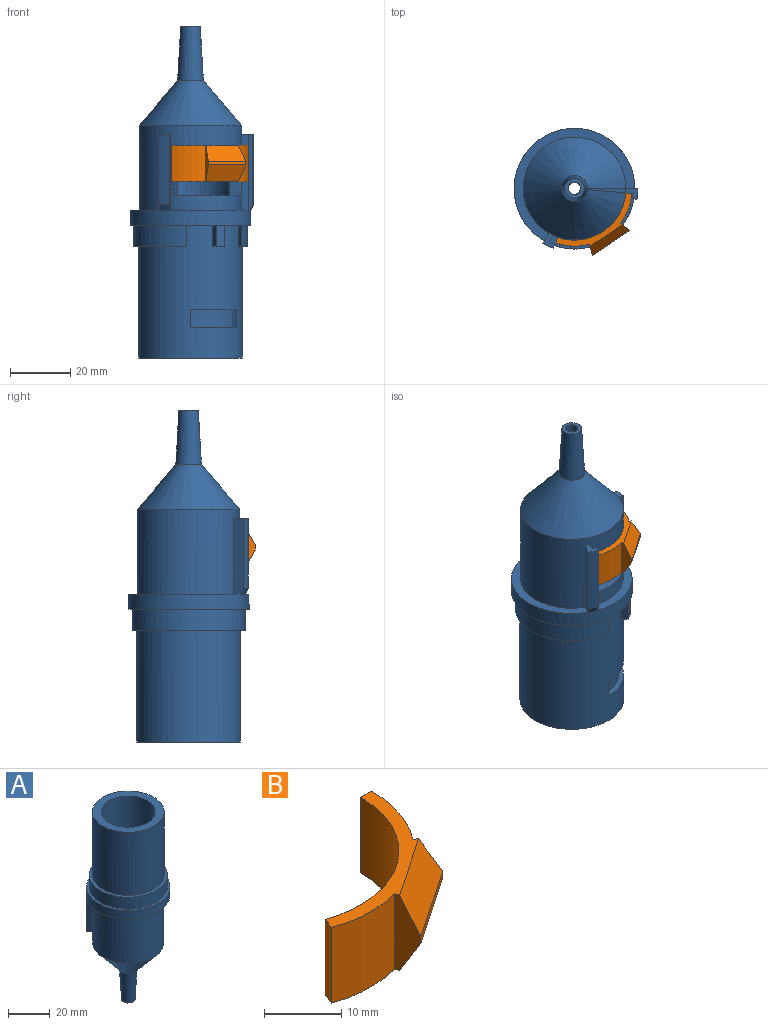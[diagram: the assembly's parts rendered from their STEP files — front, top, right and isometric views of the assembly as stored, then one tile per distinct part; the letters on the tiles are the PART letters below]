
ASSEMBLY  parts=2 mates=1
PART A: 48 faces, bbox 41x40x110 mm
  f0: plane 4.06x3.64mm, normal (0,0,-1), area 9.3mm2, adj f32,f33,f34,f35,f36,f40
  f1: plane 40x37.36mm, normal (0,0,-1), area 232.5mm2, adj f2,f18,f31,f32
  f2: cylinder r=17mm len=34mm, axis (0,0,1), area 2704.5mm2, adj f1,f19,f22,f23,f24,f25,f26,f30
  f3: plane 15.19x9.93mm, normal (0,0,1), area 29.7mm2, adj f4,f5,f6,f7
  f4: cylinder r=17.18mm len=44mm, axis (0,0,-1), area 4018.2mm2, adj f3,f5,f6,f8,f9,f10,f11,f13
  f5: plane 6x1.68mm, normal (1,0,0), area 10mm2, adj f3,f4,f7,f8
  f6: plane 6x1.48mm, normal (-0.47,0.88,0), area 10.1mm2, adj f3,f4,f7,f8
  f7: cylinder r=15.5mm len=13.7mm, axis (0,0,-1), area 100.9mm2, adj f3,f5,f6,f8
  f8: plane 15.19x9.93mm, normal (0,0,-1), area 29.7mm2, adj f4,f5,f6,f7
  f9: plane 34.35x34.35mm, normal (0,0,1), area 395.8mm2, adj f4,f21
  f10: plane 3.88x3.73mm, normal (0,0,1), area 7.6mm2, adj f4,f14,f15,f16
  f11: plane 7x1.68mm, normal (-0.86,0.5,0), area 13.6mm2, adj f4,f12,f17,f20
  f12: cylinder r=18.75mm len=37.5mm, axis (0,0,1), area 668.6mm2, adj f11,f13,f17,f20
  f13: plane 7x1.68mm, normal (0.86,-0.5,0), area 13.6mm2, adj f4,f12,f17,f20
  f14: plane 7x2.22mm, normal (-0.86,0.5,0), area 18mm2, adj f4,f10,f15,f20
  f15: plane 7x2.59mm, normal (0.5,0.86,0), area 21mm2, adj f10,f14,f16,f20
  f16: plane 7x2.22mm, normal (0.86,-0.5,0), area 18mm2, adj f4,f10,f15,f20
  f17: plane 37.5x37.46mm, normal (0,0,1), area 142.4mm2, adj f4,f11,f12,f13
  f18: cylinder r=20mm len=40mm, axis (0,0,1), area 628.3mm2, adj f1,f19,f20,f37,f38
  f19: plane 27.89x18.58mm, normal (0,0,-1), area 104.8mm2, adj f2,f18,f28,f29,f30,f33,f34,f35
  f20: plane 40x40mm, normal (0,0,1), area 179.9mm2, adj f4,f11,f12,f13,f14,f15,f16,f18
  f21: cylinder r=13mm len=74mm, axis (0,0,1), area 5885.6mm2, adj f9,f22,f23,f24,f25,f44
  f22: plane 7x3.94mm, normal (-0.17,0.99,0), area 28mm2, adj f2,f21,f24,f25
  f23: plane 7x3.76mm, normal (0.94,0.34,0), area 28mm2, adj f2,f21,f24,f25
  f24: plane 22.51x14.79mm, normal (0,0,-1), area 104.7mm2, adj f2,f21,f22,f23
  f25: plane 22.51x14.79mm, normal (0,0,1), area 104.7mm2, adj f2,f21,f22,f23
  f26: plane 5.01x3.83mm, normal (0,0,-1), area 9.3mm2, adj f2,f27,f28,f29,f30,f31
  f27: cylinder r=21mm len=23mm, axis (0,0,1), area 84.3mm2, adj f26,f28,f31,f38
  f28: plane 25x1.41mm, normal (0.94,0.34,0), area 36.5mm2, adj f19,f26,f27,f29,f38
  f29: cylinder r=19.5mm len=25mm, axis (0,0,1), area 42.5mm2, adj f19,f26,f28,f30
  f30: plane 25x2.27mm, normal (0.91,0.42,0), area 62.5mm2, adj f2,f19,f26,f29
  f31: plane 25x3.47mm, normal (-0.87,-0.5,0), area 99mm2, adj f1,f2,f26,f27,f38
  f32: plane 25x4mm, normal (0,-1,0), area 99mm2, adj f0,f1,f2,f36,f37
  f33: plane 25x2.49mm, normal (-0.08,1,0), area 62.5mm2, adj f0,f2,f19,f34
  f34: cylinder r=19.5mm len=25mm, axis (0,0,1), area 42.5mm2, adj f0,f19,f33,f35
  f35: plane 25x1.48mm, normal (-0.17,0.99,0), area 36.5mm2, adj f0,f19,f34,f36,f37
  f36: cylinder r=21mm len=23mm, axis (0,0,1), area 84.2mm2, adj f0,f32,f35,f37
  f37: cone r=21mm half-angle=26.6deg, axis (0,0,-1), area 8mm2, adj f18,f32,f35,f36
  f38: cone r=21mm half-angle=26.6deg, axis (0,0,-1), area 8mm2, adj f18,f27,f28,f31
  f39: plane 8.6x8.6mm, normal (0,0,-1), area 1.3mm2, adj f42,f43,f47
  f40: extruded ~3x1.48mm, area 4.5mm2, adj f0,f2,f43
  f41: cylinder r=3mm len=6mm, axis (0,0,-1), area 56.5mm2, adj f44,f46
  f42: cone r=4.3mm half-angle=40.3deg, axis (0,0,1), area 1296.9mm2, adj f2,f39,f43
  f43: bspline ~15x12.72mm, area 18.3mm2, adj f39,f40,f42
  f44: cone r=13mm half-angle=33.7deg, axis (0,0,1), area 906.2mm2, adj f21,f41
  f45: plane 6.5x6.5mm, normal (0,0,-1), area 20.6mm2, adj f46,f47
  f46: cone r=3mm half-angle=3.2deg, axis (0,0,1), area 283.2mm2, adj f41,f45
  f47: cone r=3.25mm half-angle=3.2deg, axis (0,0,1), area 424.8mm2, adj f39,f45
PART B: 12 faces, bbox 25.3x22.2x12 mm
  f0: cylinder r=17.1mm len=22.67mm, axis (0,0,-1), area 390.4mm2, adj f1,f7,f8,f9
  f1: plane 12x1.89mm, normal (-0.95,0.33,0), area 24mm2, adj f0,f2,f8,f9
  f2: cylinder r=19.1mm len=12mm, axis (0,0,-1), area 135.8mm2, adj f1,f3,f8,f9
  f3: plane 12x3.77mm, normal (-0.97,-0.26,0), area 29.3mm2, adj f2,f4,f8,f9,f10,f11
  f4: plane 12.44x8.38mm, normal (0.56,-0.83,0), area 15mm2, adj f3,f5,f10,f11
  f5: plane 12x3.11mm, normal (0.6,0.8,0), area 29.3mm2, adj f4,f6,f8,f9,f10,f11
  f6: cylinder r=19.1mm len=12mm, axis (0,0,-1), area 148mm2, adj f5,f7,f8,f9
  f7: plane 12x2mm, normal (0,1,0), area 24mm2, adj f0,f6,f8,f9
  f8: plane 25.32x19.16mm, normal (0,0,1), area 68.9mm2, adj f0,f1,f2,f3,f5,f6,f7,f11
  f9: plane 25.32x19.16mm, normal (0,0,-1), area 68.9mm2, adj f0,f1,f2,f3,f5,f6,f7,f10
  f10: plane 13.26x10.29mm, normal (0.49,-0.73,-0.48), area 87.5mm2, adj f3,f4,f5,f9
  f11: plane 13.26x10.29mm, normal (0.49,-0.73,0.48), area 87.5mm2, adj f3,f4,f5,f8
PLACE A rot(axis=(1,0,0),180deg) t=(0,0,37)mm
PLACE B t=(0,0,58.46)mm
MATE slider B.f0 <-> A.f2  axis (0,0,-1) through (0,0,58.46)mm
